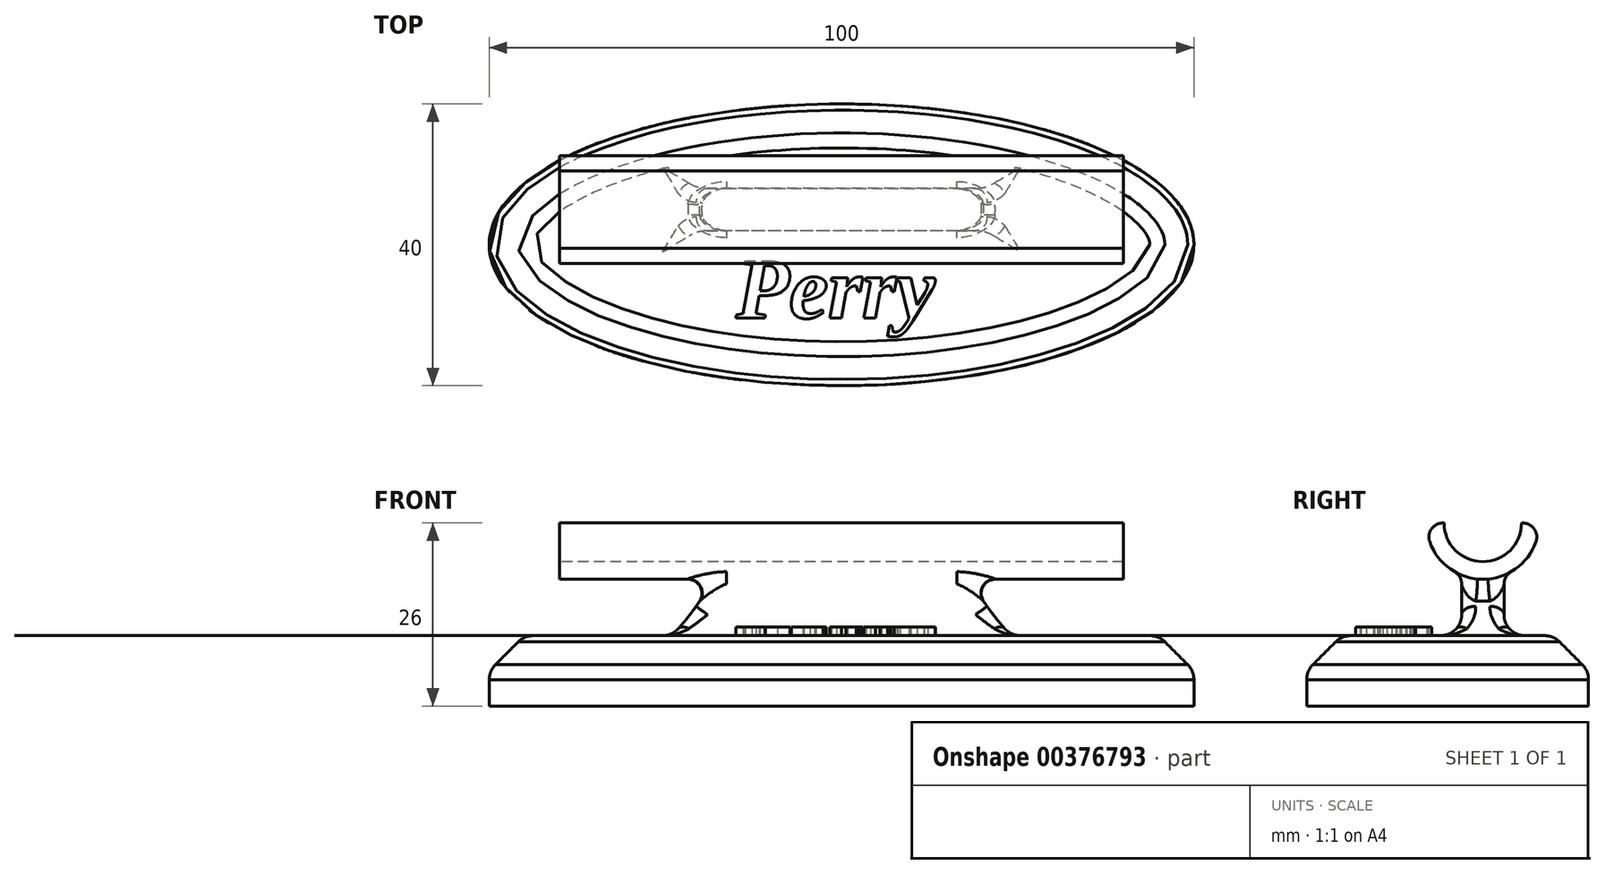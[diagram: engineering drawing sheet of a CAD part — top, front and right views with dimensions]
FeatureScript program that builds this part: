
annotation { "Feature Type Name" : "Feature", "Feature Type Description" : "" }
export const myFeature = defineFeature(function(context is Context, id is Id, definition is map)
    precondition{}
    {
        {
            var Q0;
            Q0=qCreatedBy(makeId("Top.planeOp"),FACE);
            var sketch = newSketch(context, id + "F0", { "sketchPlane" : qUnion([Q0])});
            skEllipse(sketch, "E0", {"center": v(0, 0) * mm, "majorRadius": 50 * mm, "minorRadius": 20 * mm, "majorAxis": v(1, 0)});
            skSolve(sketch);
        }
        {
            var Q0;
            Q0 = qSketchRegion(id + "F0", true);
            extrude(context, id + "F1", {"entities" : qUnion([Q0]), "depth" : 10 * mm});
        }
        {
            var Q0;
            Q0=qCreatedBy(makeId("Top.planeOp"),FACE);
            var sketch = newSketch(context, id + "F2", { "sketchPlane" : qUnion([Q0])});
            skText(sketch, "E1", { "text": "Perry", "fontName": "Tinos-BoldItalic.ttf"});
            const initialGuessF2  = {"E1": [0, 0, 1, 0, 0.0149]};
            skSetInitialGuess(sketch, initialGuessF2);
            skSolve(sketch);
        }
        {
            var Q0;
            Q0 = qSketchRegion(id + "F2", true);
            extrude(context, id + "F3", {"entities" : qUnion([Q0]), "depth" : 8 * mm});
        }
        {
            var Q0;
            Q0=makeQuery(id+"F3.opExtrude","SWEPT_BODY",BODY,{"disambiguationData":[OSD([sQuery(id+"F2.wireOp",EDGE,"E1.sketch_text.stroke-0"),sQuery(id+"F2.wireOp",EDGE,"E1.sketch_text.stroke-1"),sQuery(id+"F2.wireOp",EDGE,"E1.sketch_text.stroke-2"),sQuery(id+"F2.wireOp",EDGE,"E1.sketch_text.stroke-3"),sQuery(id+"F2.wireOp",EDGE,"E1.sketch_text.stroke-4"),sQuery(id+"F2.wireOp",EDGE,"E1.sketch_text.stroke-5"),sQuery(id+"F2.wireOp",EDGE,"E1.sketch_text.stroke-6"),sQuery(id+"F2.wireOp",EDGE,"E1.sketch_text.stroke-7"),sQuery(id+"F2.wireOp",EDGE,"E1.sketch_text.stroke-8"),sQuery(id+"F2.wireOp",EDGE,"E1.sketch_text.stroke-9"),sQuery(id+"F2.wireOp",EDGE,"E1.sketch_text.stroke-10"),sQuery(id+"F2.wireOp",EDGE,"E1.sketch_text.stroke-11"),sQuery(id+"F2.wireOp",EDGE,"E1.sketch_text.stroke-12"),sQuery(id+"F2.wireOp",EDGE,"E1.sketch_text.stroke-13"),sQuery(id+"F2.wireOp",EDGE,"E1.sketch_text.stroke-14"),sQuery(id+"F2.wireOp",EDGE,"E1.sketch_text.stroke-15"),sQuery(id+"F2.wireOp",EDGE,"E1.sketch_text.stroke-16"),sQuery(id+"F2.wireOp",EDGE,"E1.sketch_text.stroke-17"),sQuery(id+"F2.wireOp",EDGE,"E1.sketch_text.stroke-18"),sQuery(id+"F2.wireOp",EDGE,"E1.sketch_text.stroke-19"),sQuery(id+"F2.wireOp",EDGE,"E1.sketch_text.stroke-20"),sQuery(id+"F2.wireOp",EDGE,"E1.sketch_text.stroke-21")])]});
            var Q1;
            Q1=makeQuery(id+"F3.opExtrude","SWEPT_BODY",BODY,{"disambiguationData":[OSD([sQuery(id+"F2.wireOp",EDGE,"E1.sketch_text.stroke-22"),sQuery(id+"F2.wireOp",EDGE,"E1.sketch_text.stroke-23"),sQuery(id+"F2.wireOp",EDGE,"E1.sketch_text.stroke-24"),sQuery(id+"F2.wireOp",EDGE,"E1.sketch_text.stroke-25"),sQuery(id+"F2.wireOp",EDGE,"E1.sketch_text.stroke-26"),sQuery(id+"F2.wireOp",EDGE,"E1.sketch_text.stroke-27"),sQuery(id+"F2.wireOp",EDGE,"E1.sketch_text.stroke-28"),sQuery(id+"F2.wireOp",EDGE,"E1.sketch_text.stroke-29"),sQuery(id+"F2.wireOp",EDGE,"E1.sketch_text.stroke-30"),sQuery(id+"F2.wireOp",EDGE,"E1.sketch_text.stroke-31"),sQuery(id+"F2.wireOp",EDGE,"E1.sketch_text.stroke-32"),sQuery(id+"F2.wireOp",EDGE,"E1.sketch_text.stroke-33"),sQuery(id+"F2.wireOp",EDGE,"E1.sketch_text.stroke-34"),sQuery(id+"F2.wireOp",EDGE,"E1.sketch_text.stroke-35"),sQuery(id+"F2.wireOp",EDGE,"E1.sketch_text.stroke-36"),sQuery(id+"F2.wireOp",EDGE,"E1.sketch_text.stroke-37"),sQuery(id+"F2.wireOp",EDGE,"E1.sketch_text.stroke-38"),sQuery(id+"F2.wireOp",EDGE,"E1.sketch_text.stroke-39"),sQuery(id+"F2.wireOp",EDGE,"E1.sketch_text.stroke-40"),sQuery(id+"F2.wireOp",EDGE,"E1.sketch_text.stroke-41"),sQuery(id+"F2.wireOp",EDGE,"E1.sketch_text.stroke-42"),sQuery(id+"F2.wireOp",EDGE,"E1.sketch_text.stroke-43"),sQuery(id+"F2.wireOp",EDGE,"E1.sketch_text.stroke-44")])]});
            var Q2;
            Q2=makeQuery(id+"F3.opExtrude","SWEPT_BODY",BODY,{"disambiguationData":[OSD([sQuery(id+"F2.wireOp",EDGE,"E1.sketch_text.stroke-45"),sQuery(id+"F2.wireOp",EDGE,"E1.sketch_text.stroke-46"),sQuery(id+"F2.wireOp",EDGE,"E1.sketch_text.stroke-47"),sQuery(id+"F2.wireOp",EDGE,"E1.sketch_text.stroke-48"),sQuery(id+"F2.wireOp",EDGE,"E1.sketch_text.stroke-49"),sQuery(id+"F2.wireOp",EDGE,"E1.sketch_text.stroke-50"),sQuery(id+"F2.wireOp",EDGE,"E1.sketch_text.stroke-51"),sQuery(id+"F2.wireOp",EDGE,"E1.sketch_text.stroke-52"),sQuery(id+"F2.wireOp",EDGE,"E1.sketch_text.stroke-53"),sQuery(id+"F2.wireOp",EDGE,"E1.sketch_text.stroke-54"),sQuery(id+"F2.wireOp",EDGE,"E1.sketch_text.stroke-55"),sQuery(id+"F2.wireOp",EDGE,"E1.sketch_text.stroke-56"),sQuery(id+"F2.wireOp",EDGE,"E1.sketch_text.stroke-57"),sQuery(id+"F2.wireOp",EDGE,"E1.sketch_text.stroke-58"),sQuery(id+"F2.wireOp",EDGE,"E1.sketch_text.stroke-59")])]});
            var Q3;
            Q3=makeQuery(id+"F3.opExtrude","SWEPT_BODY",BODY,{"disambiguationData":[OSD([sQuery(id+"F2.wireOp",EDGE,"E1.sketch_text.stroke-60"),sQuery(id+"F2.wireOp",EDGE,"E1.sketch_text.stroke-61"),sQuery(id+"F2.wireOp",EDGE,"E1.sketch_text.stroke-62"),sQuery(id+"F2.wireOp",EDGE,"E1.sketch_text.stroke-63"),sQuery(id+"F2.wireOp",EDGE,"E1.sketch_text.stroke-64"),sQuery(id+"F2.wireOp",EDGE,"E1.sketch_text.stroke-65"),sQuery(id+"F2.wireOp",EDGE,"E1.sketch_text.stroke-66"),sQuery(id+"F2.wireOp",EDGE,"E1.sketch_text.stroke-67"),sQuery(id+"F2.wireOp",EDGE,"E1.sketch_text.stroke-68"),sQuery(id+"F2.wireOp",EDGE,"E1.sketch_text.stroke-69"),sQuery(id+"F2.wireOp",EDGE,"E1.sketch_text.stroke-70"),sQuery(id+"F2.wireOp",EDGE,"E1.sketch_text.stroke-71"),sQuery(id+"F2.wireOp",EDGE,"E1.sketch_text.stroke-72"),sQuery(id+"F2.wireOp",EDGE,"E1.sketch_text.stroke-73"),sQuery(id+"F2.wireOp",EDGE,"E1.sketch_text.stroke-74")])]});
            var Q4;
            Q4=makeQuery(id+"F3.opExtrude","SWEPT_BODY",BODY,{"disambiguationData":[OSD([sQuery(id+"F2.wireOp",EDGE,"E1.sketch_text.stroke-75"),sQuery(id+"F2.wireOp",EDGE,"E1.sketch_text.stroke-76"),sQuery(id+"F2.wireOp",EDGE,"E1.sketch_text.stroke-77"),sQuery(id+"F2.wireOp",EDGE,"E1.sketch_text.stroke-78"),sQuery(id+"F2.wireOp",EDGE,"E1.sketch_text.stroke-79"),sQuery(id+"F2.wireOp",EDGE,"E1.sketch_text.stroke-80"),sQuery(id+"F2.wireOp",EDGE,"E1.sketch_text.stroke-81"),sQuery(id+"F2.wireOp",EDGE,"E1.sketch_text.stroke-82"),sQuery(id+"F2.wireOp",EDGE,"E1.sketch_text.stroke-83"),sQuery(id+"F2.wireOp",EDGE,"E1.sketch_text.stroke-84"),sQuery(id+"F2.wireOp",EDGE,"E1.sketch_text.stroke-85"),sQuery(id+"F2.wireOp",EDGE,"E1.sketch_text.stroke-86"),sQuery(id+"F2.wireOp",EDGE,"E1.sketch_text.stroke-87"),sQuery(id+"F2.wireOp",EDGE,"E1.sketch_text.stroke-88"),sQuery(id+"F2.wireOp",EDGE,"E1.sketch_text.stroke-89"),sQuery(id+"F2.wireOp",EDGE,"E1.sketch_text.stroke-90"),sQuery(id+"F2.wireOp",EDGE,"E1.sketch_text.stroke-91"),sQuery(id+"F2.wireOp",EDGE,"E1.sketch_text.stroke-92"),sQuery(id+"F2.wireOp",EDGE,"E1.sketch_text.stroke-93"),sQuery(id+"F2.wireOp",EDGE,"E1.sketch_text.stroke-94"),sQuery(id+"F2.wireOp",EDGE,"E1.sketch_text.stroke-95"),sQuery(id+"F2.wireOp",EDGE,"E1.sketch_text.stroke-96"),sQuery(id+"F2.wireOp",EDGE,"E1.sketch_text.stroke-97"),sQuery(id+"F2.wireOp",EDGE,"E1.sketch_text.stroke-98"),sQuery(id+"F2.wireOp",EDGE,"E1.sketch_text.stroke-99"),sQuery(id+"F2.wireOp",EDGE,"E1.sketch_text.stroke-100"),sQuery(id+"F2.wireOp",EDGE,"E1.sketch_text.stroke-101")])]});
            transform(context, id + "F4", {"entities" : qUnion([Q0, Q1, Q2, Q3, Q4]), "transformType" : TransformType.TRANSLATION_3D, "dx" : 0 * mm, "dy" : 0 * mm, "dz" : 4 * mm, "makeCopy" : false});
        }
        {
            var Q0;
            Q0=makeQuery(id+"F1.opExtrude","CAP_EDGE",EDGE,{"disambiguationData":[OSD([sQuery(id+"F0.wireOp",EDGE,"E0")])],"isStart":false});
            chamfer(context, id + "F5", {"entities" : qUnion([Q0]), "width" : 5 * mm, "tangentPropagation" : true});
        }
        {
            var Q0;
            Q0=makeQuery(id+"F3.opExtrude","SWEPT_BODY",BODY,{"disambiguationData":[OSD([sQuery(id+"F2.wireOp",EDGE,"E1.sketch_text.stroke-0"),sQuery(id+"F2.wireOp",EDGE,"E1.sketch_text.stroke-1"),sQuery(id+"F2.wireOp",EDGE,"E1.sketch_text.stroke-2"),sQuery(id+"F2.wireOp",EDGE,"E1.sketch_text.stroke-3"),sQuery(id+"F2.wireOp",EDGE,"E1.sketch_text.stroke-4"),sQuery(id+"F2.wireOp",EDGE,"E1.sketch_text.stroke-5"),sQuery(id+"F2.wireOp",EDGE,"E1.sketch_text.stroke-6"),sQuery(id+"F2.wireOp",EDGE,"E1.sketch_text.stroke-7"),sQuery(id+"F2.wireOp",EDGE,"E1.sketch_text.stroke-8"),sQuery(id+"F2.wireOp",EDGE,"E1.sketch_text.stroke-9"),sQuery(id+"F2.wireOp",EDGE,"E1.sketch_text.stroke-10"),sQuery(id+"F2.wireOp",EDGE,"E1.sketch_text.stroke-11"),sQuery(id+"F2.wireOp",EDGE,"E1.sketch_text.stroke-12"),sQuery(id+"F2.wireOp",EDGE,"E1.sketch_text.stroke-13"),sQuery(id+"F2.wireOp",EDGE,"E1.sketch_text.stroke-14"),sQuery(id+"F2.wireOp",EDGE,"E1.sketch_text.stroke-15"),sQuery(id+"F2.wireOp",EDGE,"E1.sketch_text.stroke-16"),sQuery(id+"F2.wireOp",EDGE,"E1.sketch_text.stroke-17"),sQuery(id+"F2.wireOp",EDGE,"E1.sketch_text.stroke-18"),sQuery(id+"F2.wireOp",EDGE,"E1.sketch_text.stroke-19"),sQuery(id+"F2.wireOp",EDGE,"E1.sketch_text.stroke-20"),sQuery(id+"F2.wireOp",EDGE,"E1.sketch_text.stroke-21")])]});
            var Q1;
            Q1=makeQuery(id+"F3.opExtrude","SWEPT_BODY",BODY,{"disambiguationData":[OSD([sQuery(id+"F2.wireOp",EDGE,"E1.sketch_text.stroke-22"),sQuery(id+"F2.wireOp",EDGE,"E1.sketch_text.stroke-23"),sQuery(id+"F2.wireOp",EDGE,"E1.sketch_text.stroke-24"),sQuery(id+"F2.wireOp",EDGE,"E1.sketch_text.stroke-25"),sQuery(id+"F2.wireOp",EDGE,"E1.sketch_text.stroke-26"),sQuery(id+"F2.wireOp",EDGE,"E1.sketch_text.stroke-27"),sQuery(id+"F2.wireOp",EDGE,"E1.sketch_text.stroke-28"),sQuery(id+"F2.wireOp",EDGE,"E1.sketch_text.stroke-29"),sQuery(id+"F2.wireOp",EDGE,"E1.sketch_text.stroke-30"),sQuery(id+"F2.wireOp",EDGE,"E1.sketch_text.stroke-31"),sQuery(id+"F2.wireOp",EDGE,"E1.sketch_text.stroke-32"),sQuery(id+"F2.wireOp",EDGE,"E1.sketch_text.stroke-33"),sQuery(id+"F2.wireOp",EDGE,"E1.sketch_text.stroke-34"),sQuery(id+"F2.wireOp",EDGE,"E1.sketch_text.stroke-35"),sQuery(id+"F2.wireOp",EDGE,"E1.sketch_text.stroke-36"),sQuery(id+"F2.wireOp",EDGE,"E1.sketch_text.stroke-37"),sQuery(id+"F2.wireOp",EDGE,"E1.sketch_text.stroke-38"),sQuery(id+"F2.wireOp",EDGE,"E1.sketch_text.stroke-39"),sQuery(id+"F2.wireOp",EDGE,"E1.sketch_text.stroke-40"),sQuery(id+"F2.wireOp",EDGE,"E1.sketch_text.stroke-41"),sQuery(id+"F2.wireOp",EDGE,"E1.sketch_text.stroke-42"),sQuery(id+"F2.wireOp",EDGE,"E1.sketch_text.stroke-43"),sQuery(id+"F2.wireOp",EDGE,"E1.sketch_text.stroke-44")])]});
            var Q2;
            Q2=makeQuery(id+"F3.opExtrude","SWEPT_BODY",BODY,{"disambiguationData":[OSD([sQuery(id+"F2.wireOp",EDGE,"E1.sketch_text.stroke-45"),sQuery(id+"F2.wireOp",EDGE,"E1.sketch_text.stroke-46"),sQuery(id+"F2.wireOp",EDGE,"E1.sketch_text.stroke-47"),sQuery(id+"F2.wireOp",EDGE,"E1.sketch_text.stroke-48"),sQuery(id+"F2.wireOp",EDGE,"E1.sketch_text.stroke-49"),sQuery(id+"F2.wireOp",EDGE,"E1.sketch_text.stroke-50"),sQuery(id+"F2.wireOp",EDGE,"E1.sketch_text.stroke-51"),sQuery(id+"F2.wireOp",EDGE,"E1.sketch_text.stroke-52"),sQuery(id+"F2.wireOp",EDGE,"E1.sketch_text.stroke-53"),sQuery(id+"F2.wireOp",EDGE,"E1.sketch_text.stroke-54"),sQuery(id+"F2.wireOp",EDGE,"E1.sketch_text.stroke-55"),sQuery(id+"F2.wireOp",EDGE,"E1.sketch_text.stroke-56"),sQuery(id+"F2.wireOp",EDGE,"E1.sketch_text.stroke-57"),sQuery(id+"F2.wireOp",EDGE,"E1.sketch_text.stroke-58"),sQuery(id+"F2.wireOp",EDGE,"E1.sketch_text.stroke-59")])]});
            var Q3;
            Q3=makeQuery(id+"F3.opExtrude","SWEPT_BODY",BODY,{"disambiguationData":[OSD([sQuery(id+"F2.wireOp",EDGE,"E1.sketch_text.stroke-60"),sQuery(id+"F2.wireOp",EDGE,"E1.sketch_text.stroke-61"),sQuery(id+"F2.wireOp",EDGE,"E1.sketch_text.stroke-62"),sQuery(id+"F2.wireOp",EDGE,"E1.sketch_text.stroke-63"),sQuery(id+"F2.wireOp",EDGE,"E1.sketch_text.stroke-64"),sQuery(id+"F2.wireOp",EDGE,"E1.sketch_text.stroke-65"),sQuery(id+"F2.wireOp",EDGE,"E1.sketch_text.stroke-66"),sQuery(id+"F2.wireOp",EDGE,"E1.sketch_text.stroke-67"),sQuery(id+"F2.wireOp",EDGE,"E1.sketch_text.stroke-68"),sQuery(id+"F2.wireOp",EDGE,"E1.sketch_text.stroke-69"),sQuery(id+"F2.wireOp",EDGE,"E1.sketch_text.stroke-70"),sQuery(id+"F2.wireOp",EDGE,"E1.sketch_text.stroke-71"),sQuery(id+"F2.wireOp",EDGE,"E1.sketch_text.stroke-72"),sQuery(id+"F2.wireOp",EDGE,"E1.sketch_text.stroke-73"),sQuery(id+"F2.wireOp",EDGE,"E1.sketch_text.stroke-74")])]});
            var Q4;
            Q4=makeQuery(id+"F3.opExtrude","SWEPT_BODY",BODY,{"disambiguationData":[OSD([sQuery(id+"F2.wireOp",EDGE,"E1.sketch_text.stroke-75"),sQuery(id+"F2.wireOp",EDGE,"E1.sketch_text.stroke-76"),sQuery(id+"F2.wireOp",EDGE,"E1.sketch_text.stroke-77"),sQuery(id+"F2.wireOp",EDGE,"E1.sketch_text.stroke-78"),sQuery(id+"F2.wireOp",EDGE,"E1.sketch_text.stroke-79"),sQuery(id+"F2.wireOp",EDGE,"E1.sketch_text.stroke-80"),sQuery(id+"F2.wireOp",EDGE,"E1.sketch_text.stroke-81"),sQuery(id+"F2.wireOp",EDGE,"E1.sketch_text.stroke-82"),sQuery(id+"F2.wireOp",EDGE,"E1.sketch_text.stroke-83"),sQuery(id+"F2.wireOp",EDGE,"E1.sketch_text.stroke-84"),sQuery(id+"F2.wireOp",EDGE,"E1.sketch_text.stroke-85"),sQuery(id+"F2.wireOp",EDGE,"E1.sketch_text.stroke-86"),sQuery(id+"F2.wireOp",EDGE,"E1.sketch_text.stroke-87"),sQuery(id+"F2.wireOp",EDGE,"E1.sketch_text.stroke-88"),sQuery(id+"F2.wireOp",EDGE,"E1.sketch_text.stroke-89"),sQuery(id+"F2.wireOp",EDGE,"E1.sketch_text.stroke-90"),sQuery(id+"F2.wireOp",EDGE,"E1.sketch_text.stroke-91"),sQuery(id+"F2.wireOp",EDGE,"E1.sketch_text.stroke-92"),sQuery(id+"F2.wireOp",EDGE,"E1.sketch_text.stroke-93"),sQuery(id+"F2.wireOp",EDGE,"E1.sketch_text.stroke-94"),sQuery(id+"F2.wireOp",EDGE,"E1.sketch_text.stroke-95"),sQuery(id+"F2.wireOp",EDGE,"E1.sketch_text.stroke-96"),sQuery(id+"F2.wireOp",EDGE,"E1.sketch_text.stroke-97"),sQuery(id+"F2.wireOp",EDGE,"E1.sketch_text.stroke-98"),sQuery(id+"F2.wireOp",EDGE,"E1.sketch_text.stroke-99"),sQuery(id+"F2.wireOp",EDGE,"E1.sketch_text.stroke-100"),sQuery(id+"F2.wireOp",EDGE,"E1.sketch_text.stroke-101")])]});
            transform(context, id + "F6", {"entities" : qUnion([Q0, Q1, Q2, Q3, Q4]), "transformType" : TransformType.TRANSLATION_3D, "dx" : -25 * mm, "dy" : -4 * mm, "dz" : 0 * mm, "makeCopy" : false});
        }
        {
            var Q0;
            Q0=makeQuery(id+"F3.opExtrude","SWEPT_BODY",BODY,{"disambiguationData":[OSD([sQuery(id+"F2.wireOp",EDGE,"E1.sketch_text.stroke-0"),sQuery(id+"F2.wireOp",EDGE,"E1.sketch_text.stroke-1"),sQuery(id+"F2.wireOp",EDGE,"E1.sketch_text.stroke-2"),sQuery(id+"F2.wireOp",EDGE,"E1.sketch_text.stroke-3"),sQuery(id+"F2.wireOp",EDGE,"E1.sketch_text.stroke-4"),sQuery(id+"F2.wireOp",EDGE,"E1.sketch_text.stroke-5"),sQuery(id+"F2.wireOp",EDGE,"E1.sketch_text.stroke-6"),sQuery(id+"F2.wireOp",EDGE,"E1.sketch_text.stroke-7"),sQuery(id+"F2.wireOp",EDGE,"E1.sketch_text.stroke-8"),sQuery(id+"F2.wireOp",EDGE,"E1.sketch_text.stroke-9"),sQuery(id+"F2.wireOp",EDGE,"E1.sketch_text.stroke-10"),sQuery(id+"F2.wireOp",EDGE,"E1.sketch_text.stroke-11"),sQuery(id+"F2.wireOp",EDGE,"E1.sketch_text.stroke-12"),sQuery(id+"F2.wireOp",EDGE,"E1.sketch_text.stroke-13"),sQuery(id+"F2.wireOp",EDGE,"E1.sketch_text.stroke-14"),sQuery(id+"F2.wireOp",EDGE,"E1.sketch_text.stroke-15"),sQuery(id+"F2.wireOp",EDGE,"E1.sketch_text.stroke-16"),sQuery(id+"F2.wireOp",EDGE,"E1.sketch_text.stroke-17"),sQuery(id+"F2.wireOp",EDGE,"E1.sketch_text.stroke-18"),sQuery(id+"F2.wireOp",EDGE,"E1.sketch_text.stroke-19"),sQuery(id+"F2.wireOp",EDGE,"E1.sketch_text.stroke-20"),sQuery(id+"F2.wireOp",EDGE,"E1.sketch_text.stroke-21")])]});
            var Q1;
            Q1=makeQuery(id+"F3.opExtrude","SWEPT_BODY",BODY,{"disambiguationData":[OSD([sQuery(id+"F2.wireOp",EDGE,"E1.sketch_text.stroke-22"),sQuery(id+"F2.wireOp",EDGE,"E1.sketch_text.stroke-23"),sQuery(id+"F2.wireOp",EDGE,"E1.sketch_text.stroke-24"),sQuery(id+"F2.wireOp",EDGE,"E1.sketch_text.stroke-25"),sQuery(id+"F2.wireOp",EDGE,"E1.sketch_text.stroke-26"),sQuery(id+"F2.wireOp",EDGE,"E1.sketch_text.stroke-27"),sQuery(id+"F2.wireOp",EDGE,"E1.sketch_text.stroke-28"),sQuery(id+"F2.wireOp",EDGE,"E1.sketch_text.stroke-29"),sQuery(id+"F2.wireOp",EDGE,"E1.sketch_text.stroke-30"),sQuery(id+"F2.wireOp",EDGE,"E1.sketch_text.stroke-31"),sQuery(id+"F2.wireOp",EDGE,"E1.sketch_text.stroke-32"),sQuery(id+"F2.wireOp",EDGE,"E1.sketch_text.stroke-33"),sQuery(id+"F2.wireOp",EDGE,"E1.sketch_text.stroke-34"),sQuery(id+"F2.wireOp",EDGE,"E1.sketch_text.stroke-35"),sQuery(id+"F2.wireOp",EDGE,"E1.sketch_text.stroke-36"),sQuery(id+"F2.wireOp",EDGE,"E1.sketch_text.stroke-37"),sQuery(id+"F2.wireOp",EDGE,"E1.sketch_text.stroke-38"),sQuery(id+"F2.wireOp",EDGE,"E1.sketch_text.stroke-39"),sQuery(id+"F2.wireOp",EDGE,"E1.sketch_text.stroke-40"),sQuery(id+"F2.wireOp",EDGE,"E1.sketch_text.stroke-41"),sQuery(id+"F2.wireOp",EDGE,"E1.sketch_text.stroke-42"),sQuery(id+"F2.wireOp",EDGE,"E1.sketch_text.stroke-43"),sQuery(id+"F2.wireOp",EDGE,"E1.sketch_text.stroke-44")])]});
            var Q2;
            Q2=makeQuery(id+"F3.opExtrude","SWEPT_BODY",BODY,{"disambiguationData":[OSD([sQuery(id+"F2.wireOp",EDGE,"E1.sketch_text.stroke-45"),sQuery(id+"F2.wireOp",EDGE,"E1.sketch_text.stroke-46"),sQuery(id+"F2.wireOp",EDGE,"E1.sketch_text.stroke-47"),sQuery(id+"F2.wireOp",EDGE,"E1.sketch_text.stroke-48"),sQuery(id+"F2.wireOp",EDGE,"E1.sketch_text.stroke-49"),sQuery(id+"F2.wireOp",EDGE,"E1.sketch_text.stroke-50"),sQuery(id+"F2.wireOp",EDGE,"E1.sketch_text.stroke-51"),sQuery(id+"F2.wireOp",EDGE,"E1.sketch_text.stroke-52"),sQuery(id+"F2.wireOp",EDGE,"E1.sketch_text.stroke-53"),sQuery(id+"F2.wireOp",EDGE,"E1.sketch_text.stroke-54"),sQuery(id+"F2.wireOp",EDGE,"E1.sketch_text.stroke-55"),sQuery(id+"F2.wireOp",EDGE,"E1.sketch_text.stroke-56"),sQuery(id+"F2.wireOp",EDGE,"E1.sketch_text.stroke-57"),sQuery(id+"F2.wireOp",EDGE,"E1.sketch_text.stroke-58"),sQuery(id+"F2.wireOp",EDGE,"E1.sketch_text.stroke-59")])]});
            var Q3;
            Q3=makeQuery(id+"F3.opExtrude","SWEPT_BODY",BODY,{"disambiguationData":[OSD([sQuery(id+"F2.wireOp",EDGE,"E1.sketch_text.stroke-60"),sQuery(id+"F2.wireOp",EDGE,"E1.sketch_text.stroke-61"),sQuery(id+"F2.wireOp",EDGE,"E1.sketch_text.stroke-62"),sQuery(id+"F2.wireOp",EDGE,"E1.sketch_text.stroke-63"),sQuery(id+"F2.wireOp",EDGE,"E1.sketch_text.stroke-64"),sQuery(id+"F2.wireOp",EDGE,"E1.sketch_text.stroke-65"),sQuery(id+"F2.wireOp",EDGE,"E1.sketch_text.stroke-66"),sQuery(id+"F2.wireOp",EDGE,"E1.sketch_text.stroke-67"),sQuery(id+"F2.wireOp",EDGE,"E1.sketch_text.stroke-68"),sQuery(id+"F2.wireOp",EDGE,"E1.sketch_text.stroke-69"),sQuery(id+"F2.wireOp",EDGE,"E1.sketch_text.stroke-70"),sQuery(id+"F2.wireOp",EDGE,"E1.sketch_text.stroke-71"),sQuery(id+"F2.wireOp",EDGE,"E1.sketch_text.stroke-72"),sQuery(id+"F2.wireOp",EDGE,"E1.sketch_text.stroke-73"),sQuery(id+"F2.wireOp",EDGE,"E1.sketch_text.stroke-74")])]});
            var Q4;
            Q4=makeQuery(id+"F3.opExtrude","SWEPT_BODY",BODY,{"disambiguationData":[OSD([sQuery(id+"F2.wireOp",EDGE,"E1.sketch_text.stroke-75"),sQuery(id+"F2.wireOp",EDGE,"E1.sketch_text.stroke-76"),sQuery(id+"F2.wireOp",EDGE,"E1.sketch_text.stroke-77"),sQuery(id+"F2.wireOp",EDGE,"E1.sketch_text.stroke-78"),sQuery(id+"F2.wireOp",EDGE,"E1.sketch_text.stroke-79"),sQuery(id+"F2.wireOp",EDGE,"E1.sketch_text.stroke-80"),sQuery(id+"F2.wireOp",EDGE,"E1.sketch_text.stroke-81"),sQuery(id+"F2.wireOp",EDGE,"E1.sketch_text.stroke-82"),sQuery(id+"F2.wireOp",EDGE,"E1.sketch_text.stroke-83"),sQuery(id+"F2.wireOp",EDGE,"E1.sketch_text.stroke-84"),sQuery(id+"F2.wireOp",EDGE,"E1.sketch_text.stroke-85"),sQuery(id+"F2.wireOp",EDGE,"E1.sketch_text.stroke-86"),sQuery(id+"F2.wireOp",EDGE,"E1.sketch_text.stroke-87"),sQuery(id+"F2.wireOp",EDGE,"E1.sketch_text.stroke-88"),sQuery(id+"F2.wireOp",EDGE,"E1.sketch_text.stroke-89"),sQuery(id+"F2.wireOp",EDGE,"E1.sketch_text.stroke-90"),sQuery(id+"F2.wireOp",EDGE,"E1.sketch_text.stroke-91"),sQuery(id+"F2.wireOp",EDGE,"E1.sketch_text.stroke-92"),sQuery(id+"F2.wireOp",EDGE,"E1.sketch_text.stroke-93"),sQuery(id+"F2.wireOp",EDGE,"E1.sketch_text.stroke-94"),sQuery(id+"F2.wireOp",EDGE,"E1.sketch_text.stroke-95"),sQuery(id+"F2.wireOp",EDGE,"E1.sketch_text.stroke-96"),sQuery(id+"F2.wireOp",EDGE,"E1.sketch_text.stroke-97"),sQuery(id+"F2.wireOp",EDGE,"E1.sketch_text.stroke-98"),sQuery(id+"F2.wireOp",EDGE,"E1.sketch_text.stroke-99"),sQuery(id+"F2.wireOp",EDGE,"E1.sketch_text.stroke-100"),sQuery(id+"F2.wireOp",EDGE,"E1.sketch_text.stroke-101")])]});
            var Q5;
            Q5=qCreatedBy(makeId("Origin.pointOp"),VERTEX);
            transform(context, id + "F7", {"entities" : qUnion([Q0, Q1, Q2, Q3, Q4]), "transformType" : TransformType.SCALE_UNIFORMLY, "scale" : 0.6, "scalePoint" : qUnion([Q5]), "makeCopy" : false});
        }
        {
            var Q0;
            Q0=makeQuery(id+"F3.opExtrude","SWEPT_BODY",BODY,{"disambiguationData":[OSD([sQuery(id+"F2.wireOp",EDGE,"E1.sketch_text.stroke-0"),sQuery(id+"F2.wireOp",EDGE,"E1.sketch_text.stroke-1"),sQuery(id+"F2.wireOp",EDGE,"E1.sketch_text.stroke-2"),sQuery(id+"F2.wireOp",EDGE,"E1.sketch_text.stroke-3"),sQuery(id+"F2.wireOp",EDGE,"E1.sketch_text.stroke-4"),sQuery(id+"F2.wireOp",EDGE,"E1.sketch_text.stroke-5"),sQuery(id+"F2.wireOp",EDGE,"E1.sketch_text.stroke-6"),sQuery(id+"F2.wireOp",EDGE,"E1.sketch_text.stroke-7"),sQuery(id+"F2.wireOp",EDGE,"E1.sketch_text.stroke-8"),sQuery(id+"F2.wireOp",EDGE,"E1.sketch_text.stroke-9"),sQuery(id+"F2.wireOp",EDGE,"E1.sketch_text.stroke-10"),sQuery(id+"F2.wireOp",EDGE,"E1.sketch_text.stroke-11"),sQuery(id+"F2.wireOp",EDGE,"E1.sketch_text.stroke-12"),sQuery(id+"F2.wireOp",EDGE,"E1.sketch_text.stroke-13"),sQuery(id+"F2.wireOp",EDGE,"E1.sketch_text.stroke-14"),sQuery(id+"F2.wireOp",EDGE,"E1.sketch_text.stroke-15"),sQuery(id+"F2.wireOp",EDGE,"E1.sketch_text.stroke-16"),sQuery(id+"F2.wireOp",EDGE,"E1.sketch_text.stroke-17"),sQuery(id+"F2.wireOp",EDGE,"E1.sketch_text.stroke-18"),sQuery(id+"F2.wireOp",EDGE,"E1.sketch_text.stroke-19"),sQuery(id+"F2.wireOp",EDGE,"E1.sketch_text.stroke-20"),sQuery(id+"F2.wireOp",EDGE,"E1.sketch_text.stroke-21")])]});
            var Q1;
            Q1=makeQuery(id+"F3.opExtrude","SWEPT_BODY",BODY,{"disambiguationData":[OSD([sQuery(id+"F2.wireOp",EDGE,"E1.sketch_text.stroke-22"),sQuery(id+"F2.wireOp",EDGE,"E1.sketch_text.stroke-23"),sQuery(id+"F2.wireOp",EDGE,"E1.sketch_text.stroke-24"),sQuery(id+"F2.wireOp",EDGE,"E1.sketch_text.stroke-25"),sQuery(id+"F2.wireOp",EDGE,"E1.sketch_text.stroke-26"),sQuery(id+"F2.wireOp",EDGE,"E1.sketch_text.stroke-27"),sQuery(id+"F2.wireOp",EDGE,"E1.sketch_text.stroke-28"),sQuery(id+"F2.wireOp",EDGE,"E1.sketch_text.stroke-29"),sQuery(id+"F2.wireOp",EDGE,"E1.sketch_text.stroke-30"),sQuery(id+"F2.wireOp",EDGE,"E1.sketch_text.stroke-31"),sQuery(id+"F2.wireOp",EDGE,"E1.sketch_text.stroke-32"),sQuery(id+"F2.wireOp",EDGE,"E1.sketch_text.stroke-33"),sQuery(id+"F2.wireOp",EDGE,"E1.sketch_text.stroke-34"),sQuery(id+"F2.wireOp",EDGE,"E1.sketch_text.stroke-35"),sQuery(id+"F2.wireOp",EDGE,"E1.sketch_text.stroke-36"),sQuery(id+"F2.wireOp",EDGE,"E1.sketch_text.stroke-37"),sQuery(id+"F2.wireOp",EDGE,"E1.sketch_text.stroke-38"),sQuery(id+"F2.wireOp",EDGE,"E1.sketch_text.stroke-39"),sQuery(id+"F2.wireOp",EDGE,"E1.sketch_text.stroke-40"),sQuery(id+"F2.wireOp",EDGE,"E1.sketch_text.stroke-41"),sQuery(id+"F2.wireOp",EDGE,"E1.sketch_text.stroke-42"),sQuery(id+"F2.wireOp",EDGE,"E1.sketch_text.stroke-43"),sQuery(id+"F2.wireOp",EDGE,"E1.sketch_text.stroke-44")])]});
            var Q2;
            Q2=makeQuery(id+"F3.opExtrude","SWEPT_BODY",BODY,{"disambiguationData":[OSD([sQuery(id+"F2.wireOp",EDGE,"E1.sketch_text.stroke-45"),sQuery(id+"F2.wireOp",EDGE,"E1.sketch_text.stroke-46"),sQuery(id+"F2.wireOp",EDGE,"E1.sketch_text.stroke-47"),sQuery(id+"F2.wireOp",EDGE,"E1.sketch_text.stroke-48"),sQuery(id+"F2.wireOp",EDGE,"E1.sketch_text.stroke-49"),sQuery(id+"F2.wireOp",EDGE,"E1.sketch_text.stroke-50"),sQuery(id+"F2.wireOp",EDGE,"E1.sketch_text.stroke-51"),sQuery(id+"F2.wireOp",EDGE,"E1.sketch_text.stroke-52"),sQuery(id+"F2.wireOp",EDGE,"E1.sketch_text.stroke-53"),sQuery(id+"F2.wireOp",EDGE,"E1.sketch_text.stroke-54"),sQuery(id+"F2.wireOp",EDGE,"E1.sketch_text.stroke-55"),sQuery(id+"F2.wireOp",EDGE,"E1.sketch_text.stroke-56"),sQuery(id+"F2.wireOp",EDGE,"E1.sketch_text.stroke-57"),sQuery(id+"F2.wireOp",EDGE,"E1.sketch_text.stroke-58"),sQuery(id+"F2.wireOp",EDGE,"E1.sketch_text.stroke-59")])]});
            var Q3;
            Q3=makeQuery(id+"F3.opExtrude","SWEPT_BODY",BODY,{"disambiguationData":[OSD([sQuery(id+"F2.wireOp",EDGE,"E1.sketch_text.stroke-60"),sQuery(id+"F2.wireOp",EDGE,"E1.sketch_text.stroke-61"),sQuery(id+"F2.wireOp",EDGE,"E1.sketch_text.stroke-62"),sQuery(id+"F2.wireOp",EDGE,"E1.sketch_text.stroke-63"),sQuery(id+"F2.wireOp",EDGE,"E1.sketch_text.stroke-64"),sQuery(id+"F2.wireOp",EDGE,"E1.sketch_text.stroke-65"),sQuery(id+"F2.wireOp",EDGE,"E1.sketch_text.stroke-66"),sQuery(id+"F2.wireOp",EDGE,"E1.sketch_text.stroke-67"),sQuery(id+"F2.wireOp",EDGE,"E1.sketch_text.stroke-68"),sQuery(id+"F2.wireOp",EDGE,"E1.sketch_text.stroke-69"),sQuery(id+"F2.wireOp",EDGE,"E1.sketch_text.stroke-70"),sQuery(id+"F2.wireOp",EDGE,"E1.sketch_text.stroke-71"),sQuery(id+"F2.wireOp",EDGE,"E1.sketch_text.stroke-72"),sQuery(id+"F2.wireOp",EDGE,"E1.sketch_text.stroke-73"),sQuery(id+"F2.wireOp",EDGE,"E1.sketch_text.stroke-74")])]});
            var Q4;
            Q4=makeQuery(id+"F3.opExtrude","SWEPT_BODY",BODY,{"disambiguationData":[OSD([sQuery(id+"F2.wireOp",EDGE,"E1.sketch_text.stroke-75"),sQuery(id+"F2.wireOp",EDGE,"E1.sketch_text.stroke-76"),sQuery(id+"F2.wireOp",EDGE,"E1.sketch_text.stroke-77"),sQuery(id+"F2.wireOp",EDGE,"E1.sketch_text.stroke-78"),sQuery(id+"F2.wireOp",EDGE,"E1.sketch_text.stroke-79"),sQuery(id+"F2.wireOp",EDGE,"E1.sketch_text.stroke-80"),sQuery(id+"F2.wireOp",EDGE,"E1.sketch_text.stroke-81"),sQuery(id+"F2.wireOp",EDGE,"E1.sketch_text.stroke-82"),sQuery(id+"F2.wireOp",EDGE,"E1.sketch_text.stroke-83"),sQuery(id+"F2.wireOp",EDGE,"E1.sketch_text.stroke-84"),sQuery(id+"F2.wireOp",EDGE,"E1.sketch_text.stroke-85"),sQuery(id+"F2.wireOp",EDGE,"E1.sketch_text.stroke-86"),sQuery(id+"F2.wireOp",EDGE,"E1.sketch_text.stroke-87"),sQuery(id+"F2.wireOp",EDGE,"E1.sketch_text.stroke-88"),sQuery(id+"F2.wireOp",EDGE,"E1.sketch_text.stroke-89"),sQuery(id+"F2.wireOp",EDGE,"E1.sketch_text.stroke-90"),sQuery(id+"F2.wireOp",EDGE,"E1.sketch_text.stroke-91"),sQuery(id+"F2.wireOp",EDGE,"E1.sketch_text.stroke-92"),sQuery(id+"F2.wireOp",EDGE,"E1.sketch_text.stroke-93"),sQuery(id+"F2.wireOp",EDGE,"E1.sketch_text.stroke-94"),sQuery(id+"F2.wireOp",EDGE,"E1.sketch_text.stroke-95"),sQuery(id+"F2.wireOp",EDGE,"E1.sketch_text.stroke-96"),sQuery(id+"F2.wireOp",EDGE,"E1.sketch_text.stroke-97"),sQuery(id+"F2.wireOp",EDGE,"E1.sketch_text.stroke-98"),sQuery(id+"F2.wireOp",EDGE,"E1.sketch_text.stroke-99"),sQuery(id+"F2.wireOp",EDGE,"E1.sketch_text.stroke-100"),sQuery(id+"F2.wireOp",EDGE,"E1.sketch_text.stroke-101")])]});
            transform(context, id + "F8", {"entities" : qUnion([Q0, Q1, Q2, Q3, Q4]), "transformType" : TransformType.TRANSLATION_3D, "dx" : 0 * mm, "dy" : 0 * mm, "dz" : 4 * mm, "makeCopy" : false});
        }
        {
            var Q0;
            Q0=makeQuery(id+"F3.opExtrude","SWEPT_BODY",BODY,{"disambiguationData":[OSD([sQuery(id+"F2.wireOp",EDGE,"E1.sketch_text.stroke-0"),sQuery(id+"F2.wireOp",EDGE,"E1.sketch_text.stroke-1"),sQuery(id+"F2.wireOp",EDGE,"E1.sketch_text.stroke-2"),sQuery(id+"F2.wireOp",EDGE,"E1.sketch_text.stroke-3"),sQuery(id+"F2.wireOp",EDGE,"E1.sketch_text.stroke-4"),sQuery(id+"F2.wireOp",EDGE,"E1.sketch_text.stroke-5"),sQuery(id+"F2.wireOp",EDGE,"E1.sketch_text.stroke-6"),sQuery(id+"F2.wireOp",EDGE,"E1.sketch_text.stroke-7"),sQuery(id+"F2.wireOp",EDGE,"E1.sketch_text.stroke-8"),sQuery(id+"F2.wireOp",EDGE,"E1.sketch_text.stroke-9"),sQuery(id+"F2.wireOp",EDGE,"E1.sketch_text.stroke-10"),sQuery(id+"F2.wireOp",EDGE,"E1.sketch_text.stroke-11"),sQuery(id+"F2.wireOp",EDGE,"E1.sketch_text.stroke-12"),sQuery(id+"F2.wireOp",EDGE,"E1.sketch_text.stroke-13"),sQuery(id+"F2.wireOp",EDGE,"E1.sketch_text.stroke-14"),sQuery(id+"F2.wireOp",EDGE,"E1.sketch_text.stroke-15"),sQuery(id+"F2.wireOp",EDGE,"E1.sketch_text.stroke-16"),sQuery(id+"F2.wireOp",EDGE,"E1.sketch_text.stroke-17"),sQuery(id+"F2.wireOp",EDGE,"E1.sketch_text.stroke-18"),sQuery(id+"F2.wireOp",EDGE,"E1.sketch_text.stroke-19"),sQuery(id+"F2.wireOp",EDGE,"E1.sketch_text.stroke-20"),sQuery(id+"F2.wireOp",EDGE,"E1.sketch_text.stroke-21")])]});
            var Q1;
            Q1=makeQuery(id+"F3.opExtrude","SWEPT_BODY",BODY,{"disambiguationData":[OSD([sQuery(id+"F2.wireOp",EDGE,"E1.sketch_text.stroke-22"),sQuery(id+"F2.wireOp",EDGE,"E1.sketch_text.stroke-23"),sQuery(id+"F2.wireOp",EDGE,"E1.sketch_text.stroke-24"),sQuery(id+"F2.wireOp",EDGE,"E1.sketch_text.stroke-25"),sQuery(id+"F2.wireOp",EDGE,"E1.sketch_text.stroke-26"),sQuery(id+"F2.wireOp",EDGE,"E1.sketch_text.stroke-27"),sQuery(id+"F2.wireOp",EDGE,"E1.sketch_text.stroke-28"),sQuery(id+"F2.wireOp",EDGE,"E1.sketch_text.stroke-29"),sQuery(id+"F2.wireOp",EDGE,"E1.sketch_text.stroke-30"),sQuery(id+"F2.wireOp",EDGE,"E1.sketch_text.stroke-31"),sQuery(id+"F2.wireOp",EDGE,"E1.sketch_text.stroke-32"),sQuery(id+"F2.wireOp",EDGE,"E1.sketch_text.stroke-33"),sQuery(id+"F2.wireOp",EDGE,"E1.sketch_text.stroke-34"),sQuery(id+"F2.wireOp",EDGE,"E1.sketch_text.stroke-35"),sQuery(id+"F2.wireOp",EDGE,"E1.sketch_text.stroke-36"),sQuery(id+"F2.wireOp",EDGE,"E1.sketch_text.stroke-37"),sQuery(id+"F2.wireOp",EDGE,"E1.sketch_text.stroke-38"),sQuery(id+"F2.wireOp",EDGE,"E1.sketch_text.stroke-39"),sQuery(id+"F2.wireOp",EDGE,"E1.sketch_text.stroke-40"),sQuery(id+"F2.wireOp",EDGE,"E1.sketch_text.stroke-41"),sQuery(id+"F2.wireOp",EDGE,"E1.sketch_text.stroke-42"),sQuery(id+"F2.wireOp",EDGE,"E1.sketch_text.stroke-43"),sQuery(id+"F2.wireOp",EDGE,"E1.sketch_text.stroke-44")])]});
            var Q2;
            Q2=makeQuery(id+"F3.opExtrude","SWEPT_BODY",BODY,{"disambiguationData":[OSD([sQuery(id+"F2.wireOp",EDGE,"E1.sketch_text.stroke-45"),sQuery(id+"F2.wireOp",EDGE,"E1.sketch_text.stroke-46"),sQuery(id+"F2.wireOp",EDGE,"E1.sketch_text.stroke-47"),sQuery(id+"F2.wireOp",EDGE,"E1.sketch_text.stroke-48"),sQuery(id+"F2.wireOp",EDGE,"E1.sketch_text.stroke-49"),sQuery(id+"F2.wireOp",EDGE,"E1.sketch_text.stroke-50"),sQuery(id+"F2.wireOp",EDGE,"E1.sketch_text.stroke-51"),sQuery(id+"F2.wireOp",EDGE,"E1.sketch_text.stroke-52"),sQuery(id+"F2.wireOp",EDGE,"E1.sketch_text.stroke-53"),sQuery(id+"F2.wireOp",EDGE,"E1.sketch_text.stroke-54"),sQuery(id+"F2.wireOp",EDGE,"E1.sketch_text.stroke-55"),sQuery(id+"F2.wireOp",EDGE,"E1.sketch_text.stroke-56"),sQuery(id+"F2.wireOp",EDGE,"E1.sketch_text.stroke-57"),sQuery(id+"F2.wireOp",EDGE,"E1.sketch_text.stroke-58"),sQuery(id+"F2.wireOp",EDGE,"E1.sketch_text.stroke-59")])]});
            var Q3;
            Q3=makeQuery(id+"F3.opExtrude","SWEPT_BODY",BODY,{"disambiguationData":[OSD([sQuery(id+"F2.wireOp",EDGE,"E1.sketch_text.stroke-60"),sQuery(id+"F2.wireOp",EDGE,"E1.sketch_text.stroke-61"),sQuery(id+"F2.wireOp",EDGE,"E1.sketch_text.stroke-62"),sQuery(id+"F2.wireOp",EDGE,"E1.sketch_text.stroke-63"),sQuery(id+"F2.wireOp",EDGE,"E1.sketch_text.stroke-64"),sQuery(id+"F2.wireOp",EDGE,"E1.sketch_text.stroke-65"),sQuery(id+"F2.wireOp",EDGE,"E1.sketch_text.stroke-66"),sQuery(id+"F2.wireOp",EDGE,"E1.sketch_text.stroke-67"),sQuery(id+"F2.wireOp",EDGE,"E1.sketch_text.stroke-68"),sQuery(id+"F2.wireOp",EDGE,"E1.sketch_text.stroke-69"),sQuery(id+"F2.wireOp",EDGE,"E1.sketch_text.stroke-70"),sQuery(id+"F2.wireOp",EDGE,"E1.sketch_text.stroke-71"),sQuery(id+"F2.wireOp",EDGE,"E1.sketch_text.stroke-72"),sQuery(id+"F2.wireOp",EDGE,"E1.sketch_text.stroke-73"),sQuery(id+"F2.wireOp",EDGE,"E1.sketch_text.stroke-74")])]});
            var Q4;
            Q4=makeQuery(id+"F3.opExtrude","SWEPT_BODY",BODY,{"disambiguationData":[OSD([sQuery(id+"F2.wireOp",EDGE,"E1.sketch_text.stroke-75"),sQuery(id+"F2.wireOp",EDGE,"E1.sketch_text.stroke-76"),sQuery(id+"F2.wireOp",EDGE,"E1.sketch_text.stroke-77"),sQuery(id+"F2.wireOp",EDGE,"E1.sketch_text.stroke-78"),sQuery(id+"F2.wireOp",EDGE,"E1.sketch_text.stroke-79"),sQuery(id+"F2.wireOp",EDGE,"E1.sketch_text.stroke-80"),sQuery(id+"F2.wireOp",EDGE,"E1.sketch_text.stroke-81"),sQuery(id+"F2.wireOp",EDGE,"E1.sketch_text.stroke-82"),sQuery(id+"F2.wireOp",EDGE,"E1.sketch_text.stroke-83"),sQuery(id+"F2.wireOp",EDGE,"E1.sketch_text.stroke-84"),sQuery(id+"F2.wireOp",EDGE,"E1.sketch_text.stroke-85"),sQuery(id+"F2.wireOp",EDGE,"E1.sketch_text.stroke-86"),sQuery(id+"F2.wireOp",EDGE,"E1.sketch_text.stroke-87"),sQuery(id+"F2.wireOp",EDGE,"E1.sketch_text.stroke-88"),sQuery(id+"F2.wireOp",EDGE,"E1.sketch_text.stroke-89"),sQuery(id+"F2.wireOp",EDGE,"E1.sketch_text.stroke-90"),sQuery(id+"F2.wireOp",EDGE,"E1.sketch_text.stroke-91"),sQuery(id+"F2.wireOp",EDGE,"E1.sketch_text.stroke-92"),sQuery(id+"F2.wireOp",EDGE,"E1.sketch_text.stroke-93"),sQuery(id+"F2.wireOp",EDGE,"E1.sketch_text.stroke-94"),sQuery(id+"F2.wireOp",EDGE,"E1.sketch_text.stroke-95"),sQuery(id+"F2.wireOp",EDGE,"E1.sketch_text.stroke-96"),sQuery(id+"F2.wireOp",EDGE,"E1.sketch_text.stroke-97"),sQuery(id+"F2.wireOp",EDGE,"E1.sketch_text.stroke-98"),sQuery(id+"F2.wireOp",EDGE,"E1.sketch_text.stroke-99"),sQuery(id+"F2.wireOp",EDGE,"E1.sketch_text.stroke-100"),sQuery(id+"F2.wireOp",EDGE,"E1.sketch_text.stroke-101")])]});
            transform(context, id + "F9", {"entities" : qUnion([Q0, Q1, Q2, Q3, Q4]), "transformType" : TransformType.TRANSLATION_3D, "dx" : 0 * mm, "dy" : -8 * mm, "dz" : 0 * mm, "makeCopy" : false});
        }
        {
            var Q0;
            {var subQ0=sQuery(id+"F0.wireOp",EDGE,"E0");Q0=makeQuery(id+"F5.opChamfer","BLEND_EDGE",EDGE,{"blendedFrom":[makeQuery(id+"F1.opExtrude","CAP_EDGE",EDGE,{"disambiguationData":[OSD([subQ0])],"isStart":false}),makeQuery(id+"F1.opExtrude","CAP_FACE",FACE,{"disambiguationData":[OSD([subQ0])],"isStart":false})],"blendedInto":[makeQuery(id+"F1.opExtrude","CAP_FACE",FACE,{"disambiguationData":[OSD([subQ0])],"isStart":false})]});}
            var Q1;
            {var subQ0=sQuery(id+"F0.wireOp",EDGE,"E0");Q1=makeQuery(id+"F5.opChamfer","BLEND_EDGE",EDGE,{"blendedFrom":[makeQuery(id+"F1.opExtrude","CAP_EDGE",EDGE,{"disambiguationData":[OSD([subQ0])],"isStart":false}),makeQuery(id+"F1.opExtrude","SWEPT_FACE",FACE,{"disambiguationData":[OSD([subQ0])]})],"blendedInto":[makeQuery(id+"F1.opExtrude","SWEPT_FACE",FACE,{"disambiguationData":[OSD([subQ0])]})]});}
            fillet(context, id + "F10", {"entities" : qUnion([Q0, Q1]), "radius" : 3 * mm, "tangentPropagation" : true, "allowEdgeOverflow" : false});
        }
        {
            var Q0;
            Q0=qCreatedBy(makeId("Top.planeOp"),FACE);
            var sketch = newSketch(context, id + "F11", { "sketchPlane" : qUnion([Q0])});
            skLineSegment(sketch, "E2.bottom", {"start": v(25, -3) * mm, "end": v(-25, -3) * mm});
            skLineSegment(sketch, "E2.top", {"start": v(25, 3) * mm, "end": v(-25, 3) * mm});
            skLineSegment(sketch, "E2.left", {"start": v(25, -3) * mm, "end": v(25, 3) * mm});
            skLineSegment(sketch, "E2.right", {"start": v(-25, -3) * mm, "end": v(-25, 3) * mm});
            skPoint(sketch, "E2.middle", {"position": v(0, 0) * mm});
            skSolve(sketch);
        }
        {
            var Q0;
            Q0 = qSketchRegion(id + "F11", true);
            extrude(context, id + "F12", {"entities" : qUnion([Q0]), "depth" : 20 * mm});
        }
        {
            var Q0;
            Q0=qCreatedBy(makeId("Right.planeOp"),FACE);
            var sketch = newSketch(context, id + "F13", { "sketchPlane" : qUnion([Q0])});
            skArc(sketch, "E3", {"start": v(-5.5, 28) * mm, "mid": v(0, 22.5) * mm, "end": v(5.5, 28) * mm});
            skArc(sketch, "E4", {"start": v(-8, 28) * mm, "mid": v(0, 20) * mm, "end": v(8, 28) * mm});
            skLineSegment(sketch, "E5", {"start": v(5.5, 28) * mm, "end": v(8, 28) * mm});
            skLineSegment(sketch, "E6", {"start": v(-5.5, 28) * mm, "end": v(-8, 28) * mm});
            skSolve(sketch);
        }
        {
            var Q0;
            Q0 = qSketchRegion(id + "F13", true);
            extrude(context, id + "F14", {"entities" : qUnion([Q0]), "endBound" : BoundingType.SYMMETRIC, "depth" : 80 * mm});
        }
        {
            var Q0;
            Q0=makeQuery(id+"F14.opExtrude","SWEPT_BODY",BODY,{"disambiguationData":[OSD([sQuery(id+"F13.wireOp",EDGE,"E3"),sQuery(id+"F13.wireOp",EDGE,"E4"),sQuery(id+"F13.wireOp",EDGE,"E5"),sQuery(id+"F13.wireOp",EDGE,"E6")])]});
            transform(context, id + "F15", {"entities" : qUnion([Q0]), "transformType" : TransformType.TRANSLATION_3D, "dx" : 0 * mm, "dy" : 0 * mm, "dz" : -2 * mm, "makeCopy" : false});
        }
        {
            var Q0;
            Q0=qCreatedBy(makeId("Front.planeOp"),FACE);
            var sketch = newSketch(context, id + "F16", { "sketchPlane" : qUnion([Q0])});
            skLineSegment(sketch, "E7", {"start": v(0, 0) * mm, "end": v(50, 0) * mm});
            skLineSegment(sketch, "E8", {"start": v(50, 0) * mm, "end": v(50, 35) * mm});
            skCircle(sketch, "E9", {"center": v(50, 35) * mm, "radius": 36 * mm});
            skSolve(sketch);
        }
        {
            var Q0;
            Q0 = qSketchRegion(id + "F16", true);
            extrude(context, id + "F17", {"entities" : qUnion([Q0]), "endBound" : BoundingType.SYMMETRIC, "depth" : 25 * mm});
        }
        {
            var Q0;
            Q0=makeQuery(id+"F17.opExtrude","SWEPT_BODY",BODY,{"disambiguationData":[OSD([sQuery(id+"F16.wireOp",EDGE,"E9")])]});
            var Q1;
            Q1=qCreatedBy(makeId("Right.planeOp"),FACE);
            mirror(context, id + "F18", {"entities" : qUnion([Q0]), "mirrorPlane" : qUnion([Q1])});
        }
        {
            var Q0;
            Q0=makeQuery(id+"F18.opPattern","COPY",BODY,{"derivedFrom":makeQuery(id+"F17.opExtrude","SWEPT_BODY",BODY,{"disambiguationData":[OSD([sQuery(id+"F16.wireOp",EDGE,"E9")])]}),"instanceName":"1"});
            var Q1;
            Q1=makeQuery(id+"F17.opExtrude","SWEPT_BODY",BODY,{"disambiguationData":[OSD([sQuery(id+"F16.wireOp",EDGE,"E9")])]});
            var Q2;
            Q2=makeQuery(id+"F12.opExtrude","SWEPT_BODY",BODY,{"disambiguationData":[OSD([sQuery(id+"F11.wireOp",EDGE,"E2.bottom"),sQuery(id+"F11.wireOp",EDGE,"E2.top"),sQuery(id+"F11.wireOp",EDGE,"E2.left"),sQuery(id+"F11.wireOp",EDGE,"E2.right")])]});
            booleanBodies(context, id + "F19", {"operationType" : BooleanOperationType.SUBTRACTION, "tools" : qUnion([Q0, Q1]), "targets" : qUnion([Q2])});
        }
        {
            var Q0;
            Q0=makeQuery(id+"F12.opExtrude","SWEPT_BODY",BODY,{"disambiguationData":[OSD([sQuery(id+"F11.wireOp",EDGE,"E2.bottom"),sQuery(id+"F11.wireOp",EDGE,"E2.top"),sQuery(id+"F11.wireOp",EDGE,"E2.left"),sQuery(id+"F11.wireOp",EDGE,"E2.right")])]});
            var Q1;
            Q1=makeQuery(id+"F14.opExtrude","SWEPT_BODY",BODY,{"disambiguationData":[OSD([sQuery(id+"F13.wireOp",EDGE,"E3"),sQuery(id+"F13.wireOp",EDGE,"E4"),sQuery(id+"F13.wireOp",EDGE,"E5"),sQuery(id+"F13.wireOp",EDGE,"E6")])]});
            booleanBodies(context, id + "F20", {"operationType" : BooleanOperationType.UNION, "tools" : qUnion([Q0, Q1])});
        }
        {
            var Q0;
            Q0=makeQuery(id+"F3.opExtrude","SWEPT_BODY",BODY,{"disambiguationData":[OSD([sQuery(id+"F2.wireOp",EDGE,"E1.sketch_text.stroke-75"),sQuery(id+"F2.wireOp",EDGE,"E1.sketch_text.stroke-76"),sQuery(id+"F2.wireOp",EDGE,"E1.sketch_text.stroke-77"),sQuery(id+"F2.wireOp",EDGE,"E1.sketch_text.stroke-78"),sQuery(id+"F2.wireOp",EDGE,"E1.sketch_text.stroke-79"),sQuery(id+"F2.wireOp",EDGE,"E1.sketch_text.stroke-80"),sQuery(id+"F2.wireOp",EDGE,"E1.sketch_text.stroke-81"),sQuery(id+"F2.wireOp",EDGE,"E1.sketch_text.stroke-82"),sQuery(id+"F2.wireOp",EDGE,"E1.sketch_text.stroke-83"),sQuery(id+"F2.wireOp",EDGE,"E1.sketch_text.stroke-84"),sQuery(id+"F2.wireOp",EDGE,"E1.sketch_text.stroke-85"),sQuery(id+"F2.wireOp",EDGE,"E1.sketch_text.stroke-86"),sQuery(id+"F2.wireOp",EDGE,"E1.sketch_text.stroke-87"),sQuery(id+"F2.wireOp",EDGE,"E1.sketch_text.stroke-88"),sQuery(id+"F2.wireOp",EDGE,"E1.sketch_text.stroke-89"),sQuery(id+"F2.wireOp",EDGE,"E1.sketch_text.stroke-90"),sQuery(id+"F2.wireOp",EDGE,"E1.sketch_text.stroke-91"),sQuery(id+"F2.wireOp",EDGE,"E1.sketch_text.stroke-92"),sQuery(id+"F2.wireOp",EDGE,"E1.sketch_text.stroke-93"),sQuery(id+"F2.wireOp",EDGE,"E1.sketch_text.stroke-94"),sQuery(id+"F2.wireOp",EDGE,"E1.sketch_text.stroke-95"),sQuery(id+"F2.wireOp",EDGE,"E1.sketch_text.stroke-96"),sQuery(id+"F2.wireOp",EDGE,"E1.sketch_text.stroke-97"),sQuery(id+"F2.wireOp",EDGE,"E1.sketch_text.stroke-98"),sQuery(id+"F2.wireOp",EDGE,"E1.sketch_text.stroke-99"),sQuery(id+"F2.wireOp",EDGE,"E1.sketch_text.stroke-100"),sQuery(id+"F2.wireOp",EDGE,"E1.sketch_text.stroke-101")])]});
            var Q1;
            Q1=makeQuery(id+"F3.opExtrude","SWEPT_BODY",BODY,{"disambiguationData":[OSD([sQuery(id+"F2.wireOp",EDGE,"E1.sketch_text.stroke-60"),sQuery(id+"F2.wireOp",EDGE,"E1.sketch_text.stroke-61"),sQuery(id+"F2.wireOp",EDGE,"E1.sketch_text.stroke-62"),sQuery(id+"F2.wireOp",EDGE,"E1.sketch_text.stroke-63"),sQuery(id+"F2.wireOp",EDGE,"E1.sketch_text.stroke-64"),sQuery(id+"F2.wireOp",EDGE,"E1.sketch_text.stroke-65"),sQuery(id+"F2.wireOp",EDGE,"E1.sketch_text.stroke-66"),sQuery(id+"F2.wireOp",EDGE,"E1.sketch_text.stroke-67"),sQuery(id+"F2.wireOp",EDGE,"E1.sketch_text.stroke-68"),sQuery(id+"F2.wireOp",EDGE,"E1.sketch_text.stroke-69"),sQuery(id+"F2.wireOp",EDGE,"E1.sketch_text.stroke-70"),sQuery(id+"F2.wireOp",EDGE,"E1.sketch_text.stroke-71"),sQuery(id+"F2.wireOp",EDGE,"E1.sketch_text.stroke-72"),sQuery(id+"F2.wireOp",EDGE,"E1.sketch_text.stroke-73"),sQuery(id+"F2.wireOp",EDGE,"E1.sketch_text.stroke-74")])]});
            var Q2;
            Q2=makeQuery(id+"F3.opExtrude","SWEPT_BODY",BODY,{"disambiguationData":[OSD([sQuery(id+"F2.wireOp",EDGE,"E1.sketch_text.stroke-45"),sQuery(id+"F2.wireOp",EDGE,"E1.sketch_text.stroke-46"),sQuery(id+"F2.wireOp",EDGE,"E1.sketch_text.stroke-47"),sQuery(id+"F2.wireOp",EDGE,"E1.sketch_text.stroke-48"),sQuery(id+"F2.wireOp",EDGE,"E1.sketch_text.stroke-49"),sQuery(id+"F2.wireOp",EDGE,"E1.sketch_text.stroke-50"),sQuery(id+"F2.wireOp",EDGE,"E1.sketch_text.stroke-51"),sQuery(id+"F2.wireOp",EDGE,"E1.sketch_text.stroke-52"),sQuery(id+"F2.wireOp",EDGE,"E1.sketch_text.stroke-53"),sQuery(id+"F2.wireOp",EDGE,"E1.sketch_text.stroke-54"),sQuery(id+"F2.wireOp",EDGE,"E1.sketch_text.stroke-55"),sQuery(id+"F2.wireOp",EDGE,"E1.sketch_text.stroke-56"),sQuery(id+"F2.wireOp",EDGE,"E1.sketch_text.stroke-57"),sQuery(id+"F2.wireOp",EDGE,"E1.sketch_text.stroke-58"),sQuery(id+"F2.wireOp",EDGE,"E1.sketch_text.stroke-59")])]});
            var Q3;
            Q3=makeQuery(id+"F3.opExtrude","SWEPT_BODY",BODY,{"disambiguationData":[OSD([sQuery(id+"F2.wireOp",EDGE,"E1.sketch_text.stroke-22"),sQuery(id+"F2.wireOp",EDGE,"E1.sketch_text.stroke-23"),sQuery(id+"F2.wireOp",EDGE,"E1.sketch_text.stroke-24"),sQuery(id+"F2.wireOp",EDGE,"E1.sketch_text.stroke-25"),sQuery(id+"F2.wireOp",EDGE,"E1.sketch_text.stroke-26"),sQuery(id+"F2.wireOp",EDGE,"E1.sketch_text.stroke-27"),sQuery(id+"F2.wireOp",EDGE,"E1.sketch_text.stroke-28"),sQuery(id+"F2.wireOp",EDGE,"E1.sketch_text.stroke-29"),sQuery(id+"F2.wireOp",EDGE,"E1.sketch_text.stroke-30"),sQuery(id+"F2.wireOp",EDGE,"E1.sketch_text.stroke-31"),sQuery(id+"F2.wireOp",EDGE,"E1.sketch_text.stroke-32"),sQuery(id+"F2.wireOp",EDGE,"E1.sketch_text.stroke-33"),sQuery(id+"F2.wireOp",EDGE,"E1.sketch_text.stroke-34"),sQuery(id+"F2.wireOp",EDGE,"E1.sketch_text.stroke-35"),sQuery(id+"F2.wireOp",EDGE,"E1.sketch_text.stroke-36"),sQuery(id+"F2.wireOp",EDGE,"E1.sketch_text.stroke-37"),sQuery(id+"F2.wireOp",EDGE,"E1.sketch_text.stroke-38"),sQuery(id+"F2.wireOp",EDGE,"E1.sketch_text.stroke-39"),sQuery(id+"F2.wireOp",EDGE,"E1.sketch_text.stroke-40"),sQuery(id+"F2.wireOp",EDGE,"E1.sketch_text.stroke-41"),sQuery(id+"F2.wireOp",EDGE,"E1.sketch_text.stroke-42"),sQuery(id+"F2.wireOp",EDGE,"E1.sketch_text.stroke-43"),sQuery(id+"F2.wireOp",EDGE,"E1.sketch_text.stroke-44")])]});
            var Q4;
            Q4=makeQuery(id+"F3.opExtrude","SWEPT_BODY",BODY,{"disambiguationData":[OSD([sQuery(id+"F2.wireOp",EDGE,"E1.sketch_text.stroke-0"),sQuery(id+"F2.wireOp",EDGE,"E1.sketch_text.stroke-1"),sQuery(id+"F2.wireOp",EDGE,"E1.sketch_text.stroke-2"),sQuery(id+"F2.wireOp",EDGE,"E1.sketch_text.stroke-3"),sQuery(id+"F2.wireOp",EDGE,"E1.sketch_text.stroke-4"),sQuery(id+"F2.wireOp",EDGE,"E1.sketch_text.stroke-5"),sQuery(id+"F2.wireOp",EDGE,"E1.sketch_text.stroke-6"),sQuery(id+"F2.wireOp",EDGE,"E1.sketch_text.stroke-7"),sQuery(id+"F2.wireOp",EDGE,"E1.sketch_text.stroke-8"),sQuery(id+"F2.wireOp",EDGE,"E1.sketch_text.stroke-9"),sQuery(id+"F2.wireOp",EDGE,"E1.sketch_text.stroke-10"),sQuery(id+"F2.wireOp",EDGE,"E1.sketch_text.stroke-11"),sQuery(id+"F2.wireOp",EDGE,"E1.sketch_text.stroke-12"),sQuery(id+"F2.wireOp",EDGE,"E1.sketch_text.stroke-13"),sQuery(id+"F2.wireOp",EDGE,"E1.sketch_text.stroke-14"),sQuery(id+"F2.wireOp",EDGE,"E1.sketch_text.stroke-15"),sQuery(id+"F2.wireOp",EDGE,"E1.sketch_text.stroke-16"),sQuery(id+"F2.wireOp",EDGE,"E1.sketch_text.stroke-17"),sQuery(id+"F2.wireOp",EDGE,"E1.sketch_text.stroke-18"),sQuery(id+"F2.wireOp",EDGE,"E1.sketch_text.stroke-19"),sQuery(id+"F2.wireOp",EDGE,"E1.sketch_text.stroke-20"),sQuery(id+"F2.wireOp",EDGE,"E1.sketch_text.stroke-21")])]});
            var Q5;
            Q5=makeQuery(id+"F1.opExtrude","SWEPT_BODY",BODY,{"disambiguationData":[OSD([sQuery(id+"F0.wireOp",EDGE,"E0")])]});
            booleanBodies(context, id + "F21", {"operationType" : BooleanOperationType.UNION, "tools" : qUnion([Q0, Q1, Q2, Q3, Q4, Q5])});
        }
        {
            var Q0;
            Q0=makeQuery(id+"F12.opExtrude","SWEPT_BODY",BODY,{"disambiguationData":[OSD([sQuery(id+"F11.wireOp",EDGE,"E2.bottom"),sQuery(id+"F11.wireOp",EDGE,"E2.top"),sQuery(id+"F11.wireOp",EDGE,"E2.left"),sQuery(id+"F11.wireOp",EDGE,"E2.right")])]});
            transform(context, id + "F22", {"entities" : qUnion([Q0]), "transformType" : TransformType.TRANSLATION_3D, "dx" : 0 * mm, "dy" : 5 * mm, "dz" : 0 * mm, "makeCopy" : false});
        }
        {
            var Q0;
            Q0=makeQuery(id+"F12.opExtrude","SWEPT_BODY",BODY,{"disambiguationData":[OSD([sQuery(id+"F11.wireOp",EDGE,"E2.bottom"),sQuery(id+"F11.wireOp",EDGE,"E2.top"),sQuery(id+"F11.wireOp",EDGE,"E2.left"),sQuery(id+"F11.wireOp",EDGE,"E2.right")])]});
            var Q1;
            Q1=makeQuery(id+"F3.opExtrude","SWEPT_BODY",BODY,{"disambiguationData":[OSD([sQuery(id+"F2.wireOp",EDGE,"E1.sketch_text.stroke-75"),sQuery(id+"F2.wireOp",EDGE,"E1.sketch_text.stroke-76"),sQuery(id+"F2.wireOp",EDGE,"E1.sketch_text.stroke-77"),sQuery(id+"F2.wireOp",EDGE,"E1.sketch_text.stroke-78"),sQuery(id+"F2.wireOp",EDGE,"E1.sketch_text.stroke-79"),sQuery(id+"F2.wireOp",EDGE,"E1.sketch_text.stroke-80"),sQuery(id+"F2.wireOp",EDGE,"E1.sketch_text.stroke-81"),sQuery(id+"F2.wireOp",EDGE,"E1.sketch_text.stroke-82"),sQuery(id+"F2.wireOp",EDGE,"E1.sketch_text.stroke-83"),sQuery(id+"F2.wireOp",EDGE,"E1.sketch_text.stroke-84"),sQuery(id+"F2.wireOp",EDGE,"E1.sketch_text.stroke-85"),sQuery(id+"F2.wireOp",EDGE,"E1.sketch_text.stroke-86"),sQuery(id+"F2.wireOp",EDGE,"E1.sketch_text.stroke-87"),sQuery(id+"F2.wireOp",EDGE,"E1.sketch_text.stroke-88"),sQuery(id+"F2.wireOp",EDGE,"E1.sketch_text.stroke-89"),sQuery(id+"F2.wireOp",EDGE,"E1.sketch_text.stroke-90"),sQuery(id+"F2.wireOp",EDGE,"E1.sketch_text.stroke-91"),sQuery(id+"F2.wireOp",EDGE,"E1.sketch_text.stroke-92"),sQuery(id+"F2.wireOp",EDGE,"E1.sketch_text.stroke-93"),sQuery(id+"F2.wireOp",EDGE,"E1.sketch_text.stroke-94"),sQuery(id+"F2.wireOp",EDGE,"E1.sketch_text.stroke-95"),sQuery(id+"F2.wireOp",EDGE,"E1.sketch_text.stroke-96"),sQuery(id+"F2.wireOp",EDGE,"E1.sketch_text.stroke-97"),sQuery(id+"F2.wireOp",EDGE,"E1.sketch_text.stroke-98"),sQuery(id+"F2.wireOp",EDGE,"E1.sketch_text.stroke-99"),sQuery(id+"F2.wireOp",EDGE,"E1.sketch_text.stroke-100"),sQuery(id+"F2.wireOp",EDGE,"E1.sketch_text.stroke-101")])]});
            booleanBodies(context, id + "F23", {"operationType" : BooleanOperationType.UNION, "tools" : qUnion([Q0, Q1])});
        }
        {
            var Q0;
            {var subQ0=sQuery(id+"F0.wireOp",EDGE,"E0");var subQ1=makeQuery(id+"F1.opExtrude","CAP_FACE",FACE,{"disambiguationData":[OSD([subQ0])],"isStart":false});Q0=makeQuery(id+"F23.opBoolean","INTERSECT",EDGE,{"derivedFrom":[makeQuery(id+"F12.opExtrude","SWEPT_FACE",FACE,{"disambiguationData":[OSD([sQuery(id+"F11.wireOp",EDGE,"E2.bottom")])]}),makeQuery(id+"F21.opBoolean","SPLIT",FACE,{"disambiguationData":[TD([makeQuery(id+"F3.opExtrude","SWEPT_FACE",FACE,{"disambiguationData":[OSD([sQuery(id+"F2.wireOp",EDGE,"E1.sketch_text.stroke-7")])]})])],"derivedFrom":subQ1})]});}
            var Q1;
            {var subQ0=sQuery(id+"F0.wireOp",EDGE,"E0");var subQ1=makeQuery(id+"F1.opExtrude","CAP_FACE",FACE,{"disambiguationData":[OSD([subQ0])],"isStart":false});Q1=makeQuery(id+"F23.opBoolean","INTERSECT",EDGE,{"derivedFrom":[makeQuery(id+"F12.opExtrude","SWEPT_FACE",FACE,{"disambiguationData":[OSD([sQuery(id+"F11.wireOp",EDGE,"E2.top")])]}),makeQuery(id+"F21.opBoolean","SPLIT",FACE,{"disambiguationData":[TD([makeQuery(id+"F3.opExtrude","SWEPT_FACE",FACE,{"disambiguationData":[OSD([sQuery(id+"F2.wireOp",EDGE,"E1.sketch_text.stroke-7")])]})])],"derivedFrom":subQ1})]});}
            var Q2;
            {var subQ0=sQuery(id+"F0.wireOp",EDGE,"E0");var subQ1=makeQuery(id+"F1.opExtrude","CAP_FACE",FACE,{"disambiguationData":[OSD([subQ0])],"isStart":false});Q2=makeQuery(id+"F23.opBoolean","INTERSECT",EDGE,{"derivedFrom":[makeQuery(id+"F19.opBoolean","COPY",FACE,{"derivedFrom":makeQuery(id+"F17.opExtrude","SWEPT_FACE",FACE,{"disambiguationData":[OSD([sQuery(id+"F16.wireOp",EDGE,"E9")])]})}),makeQuery(id+"F21.opBoolean","SPLIT",FACE,{"disambiguationData":[TD([makeQuery(id+"F3.opExtrude","SWEPT_FACE",FACE,{"disambiguationData":[OSD([sQuery(id+"F2.wireOp",EDGE,"E1.sketch_text.stroke-7")])]})])],"derivedFrom":subQ1})]});}
            var Q3;
            {var subQ0=sQuery(id+"F0.wireOp",EDGE,"E0");var subQ1=makeQuery(id+"F1.opExtrude","CAP_FACE",FACE,{"disambiguationData":[OSD([subQ0])],"isStart":false});Q3=makeQuery(id+"F23.opBoolean","INTERSECT",EDGE,{"derivedFrom":[makeQuery(id+"F19.opBoolean","COPY",FACE,{"derivedFrom":makeQuery(id+"F18.opPattern","COPY",FACE,{"derivedFrom":makeQuery(id+"F17.opExtrude","SWEPT_FACE",FACE,{"disambiguationData":[OSD([sQuery(id+"F16.wireOp",EDGE,"E9")])]}),"instanceName":"1"})}),makeQuery(id+"F21.opBoolean","SPLIT",FACE,{"disambiguationData":[TD([makeQuery(id+"F3.opExtrude","SWEPT_FACE",FACE,{"disambiguationData":[OSD([sQuery(id+"F2.wireOp",EDGE,"E1.sketch_text.stroke-7")])]})])],"derivedFrom":subQ1})]});}
            fillet(context, id + "F24", {"entities" : qUnion([Q0, Q1, Q2, Q3]), "radius" : 3 * mm, "tangentPropagation" : true, "allowEdgeOverflow" : false});
        }
        {
            var Q0;
            Q0=makeQuery(id+"F14.opExtrude","SWEPT_EDGE",EDGE,{"disambiguationData":[OSD([sQuery(id+"F13.wireOp",EDGE,"E4"),sQuery(id+"F13.wireOp",EDGE,"E6")])]});
            var Q1;
            Q1=makeQuery(id+"F14.opExtrude","SWEPT_EDGE",EDGE,{"disambiguationData":[OSD([sQuery(id+"F13.wireOp",EDGE,"E4"),sQuery(id+"F13.wireOp",EDGE,"E5")])]});
            fillet(context, id + "F25", {"entities" : qUnion([Q0, Q1]), "radius" : 2 * mm, "tangentPropagation" : true, "allowEdgeOverflow" : false});
        }
        {
            var Q0;
            Q0=makeQuery(id+"F20.opBoolean","INTERSECT",EDGE,{"derivedFrom":[makeQuery(id+"F14.opExtrude","SWEPT_FACE",FACE,{"disambiguationData":[OSD([sQuery(id+"F13.wireOp",EDGE,"E4")])]}),makeQuery(id+"F19.opBoolean","COPY",FACE,{"derivedFrom":makeQuery(id+"F18.opPattern","COPY",FACE,{"derivedFrom":makeQuery(id+"F17.opExtrude","SWEPT_FACE",FACE,{"disambiguationData":[OSD([sQuery(id+"F16.wireOp",EDGE,"E9")])]}),"instanceName":"1"})})]});
            var Q1;
            Q1=makeQuery(id+"F20.opBoolean","INTERSECT",EDGE,{"derivedFrom":[makeQuery(id+"F14.opExtrude","SWEPT_FACE",FACE,{"disambiguationData":[OSD([sQuery(id+"F13.wireOp",EDGE,"E4")])]}),makeQuery(id+"F19.opBoolean","COPY",FACE,{"derivedFrom":makeQuery(id+"F17.opExtrude","SWEPT_FACE",FACE,{"disambiguationData":[OSD([sQuery(id+"F16.wireOp",EDGE,"E9")])]})})]});
            fillet(context, id + "F26", {"entities" : qUnion([Q0, Q1]), "radius" : 2 * mm, "tangentPropagation" : true, "allowEdgeOverflow" : false});
        }
        {
            var Q0;
            Q0=makeQuery(id+"F20.opBoolean","INTERSECT",EDGE,{"derivedFrom":[makeQuery(id+"F14.opExtrude","SWEPT_FACE",FACE,{"disambiguationData":[OSD([sQuery(id+"F13.wireOp",EDGE,"E4")])]}),makeQuery(id+"F12.opExtrude","SWEPT_FACE",FACE,{"disambiguationData":[OSD([sQuery(id+"F11.wireOp",EDGE,"E2.bottom")])]})]});
            var Q1;
            Q1=makeQuery(id+"F20.opBoolean","INTERSECT",EDGE,{"derivedFrom":[makeQuery(id+"F14.opExtrude","SWEPT_FACE",FACE,{"disambiguationData":[OSD([sQuery(id+"F13.wireOp",EDGE,"E4")])]}),makeQuery(id+"F12.opExtrude","SWEPT_FACE",FACE,{"disambiguationData":[OSD([sQuery(id+"F11.wireOp",EDGE,"E2.top")])]})]});
            var Q2;
            Q2=makeQuery(id+"F19.opBoolean","INTERSECT",EDGE,{"derivedFrom":[makeQuery(id+"F12.opExtrude","SWEPT_FACE",FACE,{"disambiguationData":[OSD([sQuery(id+"F11.wireOp",EDGE,"E2.bottom")])]}),makeQuery(id+"F18.opPattern","COPY",FACE,{"derivedFrom":makeQuery(id+"F17.opExtrude","SWEPT_FACE",FACE,{"disambiguationData":[OSD([sQuery(id+"F16.wireOp",EDGE,"E9")])]}),"instanceName":"1"})]});
            var Q3;
            Q3=makeQuery(id+"F19.opBoolean","INTERSECT",EDGE,{"derivedFrom":[makeQuery(id+"F12.opExtrude","SWEPT_FACE",FACE,{"disambiguationData":[OSD([sQuery(id+"F11.wireOp",EDGE,"E2.top")])]}),makeQuery(id+"F18.opPattern","COPY",FACE,{"derivedFrom":makeQuery(id+"F17.opExtrude","SWEPT_FACE",FACE,{"disambiguationData":[OSD([sQuery(id+"F16.wireOp",EDGE,"E9")])]}),"instanceName":"1"})]});
            var Q4;
            Q4=makeQuery(id+"F19.opBoolean","INTERSECT",EDGE,{"derivedFrom":[makeQuery(id+"F12.opExtrude","SWEPT_FACE",FACE,{"disambiguationData":[OSD([sQuery(id+"F11.wireOp",EDGE,"E2.top")])]}),makeQuery(id+"F17.opExtrude","SWEPT_FACE",FACE,{"disambiguationData":[OSD([sQuery(id+"F16.wireOp",EDGE,"E9")])]})]});
            var Q5;
            Q5=makeQuery(id+"F19.opBoolean","INTERSECT",EDGE,{"derivedFrom":[makeQuery(id+"F12.opExtrude","SWEPT_FACE",FACE,{"disambiguationData":[OSD([sQuery(id+"F11.wireOp",EDGE,"E2.bottom")])]}),makeQuery(id+"F17.opExtrude","SWEPT_FACE",FACE,{"disambiguationData":[OSD([sQuery(id+"F16.wireOp",EDGE,"E9")])]})]});
            fillet(context, id + "F27", {"entities" : qUnion([Q0, Q1, Q2, Q3, Q4, Q5]), "radius" : 2 * mm, "tangentPropagation" : true, "allowEdgeOverflow" : false});
        }
    });
